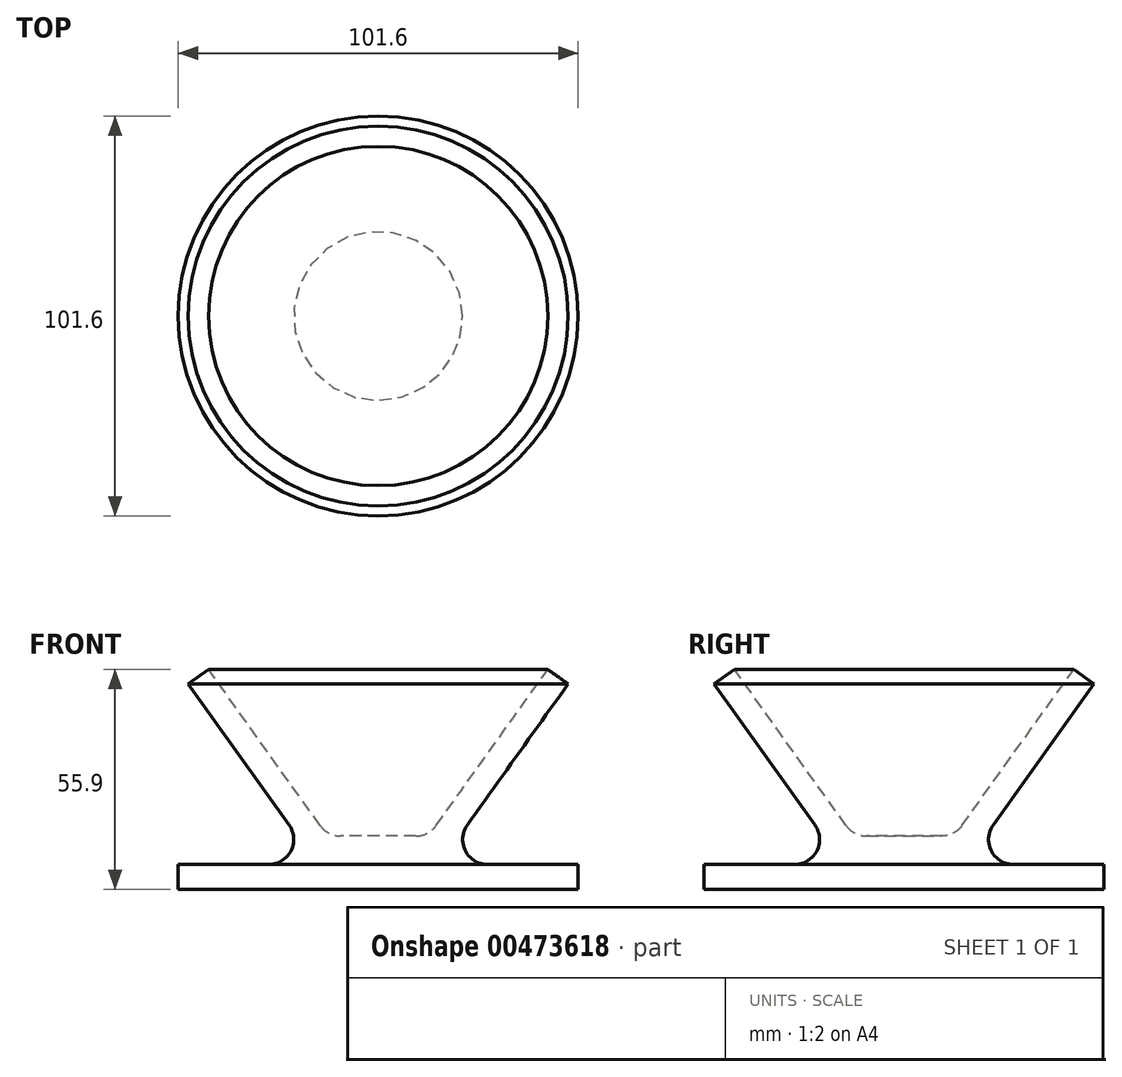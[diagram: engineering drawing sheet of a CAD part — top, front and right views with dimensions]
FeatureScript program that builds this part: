
annotation { "Feature Type Name" : "Feature", "Feature Type Description" : "" }
export const myFeature = defineFeature(function(context is Context, id is Id, definition is map)
    precondition{}
    {
        {
            var Q0;
            Q0=qCreatedBy(makeId("Front.planeOp"),FACE);
            var sketch = newSketch(context, id + "F0", { "sketchPlane" : qUnion([Q0])});
            skLineSegment(sketch, "E0", {"start": v(0, 0) * mm, "end": v(50.8, 0) * mm});
            skLineSegment(sketch, "E1", {"start": v(50.8, 0) * mm, "end": v(50.8, 6.35) * mm});
            skLineSegment(sketch, "E2", {"start": v(50.8, 6.35) * mm, "end": v(27.81, 6.35) * mm});
            skLineSegment(sketch, "E3", {"start": v(22.65, 16.4) * mm, "end": v(48.27, 52.2) * mm});
            skLineSegment(sketch, "E4", {"start": v(48.27, 52.2) * mm, "end": v(43.1, 55.9) * mm});
            skLineSegment(sketch, "E5", {"start": v(43.1, 55.9) * mm, "end": v(14.72, 16.22) * mm});
            skLineSegment(sketch, "E6", {"start": v(9.55, 13.57) * mm, "end": v(0, 13.57) * mm});
            skLineSegment(sketch, "E7", {"start": v(0, 13.57) * mm, "end": v(0, 0) * mm});
            skPoint(sketch, "E8.visualSharp", {"position": v(15.46, 6.35) * mm});
            skArc(sketch, "E8.filletArc", {"start": v(22.65, 16.4) * mm, "mid": v(22.16, 9.8) * mm, "end": v(27.81, 6.35) * mm});
            skPoint(sketch, "E9.visualSharp", {"position": v(12.82, 13.57) * mm});
            skArc(sketch, "E9.filletArc", {"start": v(9.55, 13.57) * mm, "mid": v(12.45, 14.27) * mm, "end": v(14.72, 16.22) * mm});
            skSolve(sketch);
        }
        {
            var Q0;
            Q0=makeQuery(id+"F0.imprint","IMPRINT",FACE,{"disambiguationData":[TD([[makeQuery(id+"F0.imprint","IMPRINT",EDGE,{"derivedFrom":sQuery(id+"F0.wireOp",EDGE,"E0")}),1.0]])]});
            var Q1;
            Q1=sQuery(id+"F0.wireOp",EDGE,"E7");
            revolve(context, id + "F1", {"entities" : qUnion([Q0]), "axis" : qUnion([Q1]), "revolveType" : RevolveType.FULL});
        }
    });
